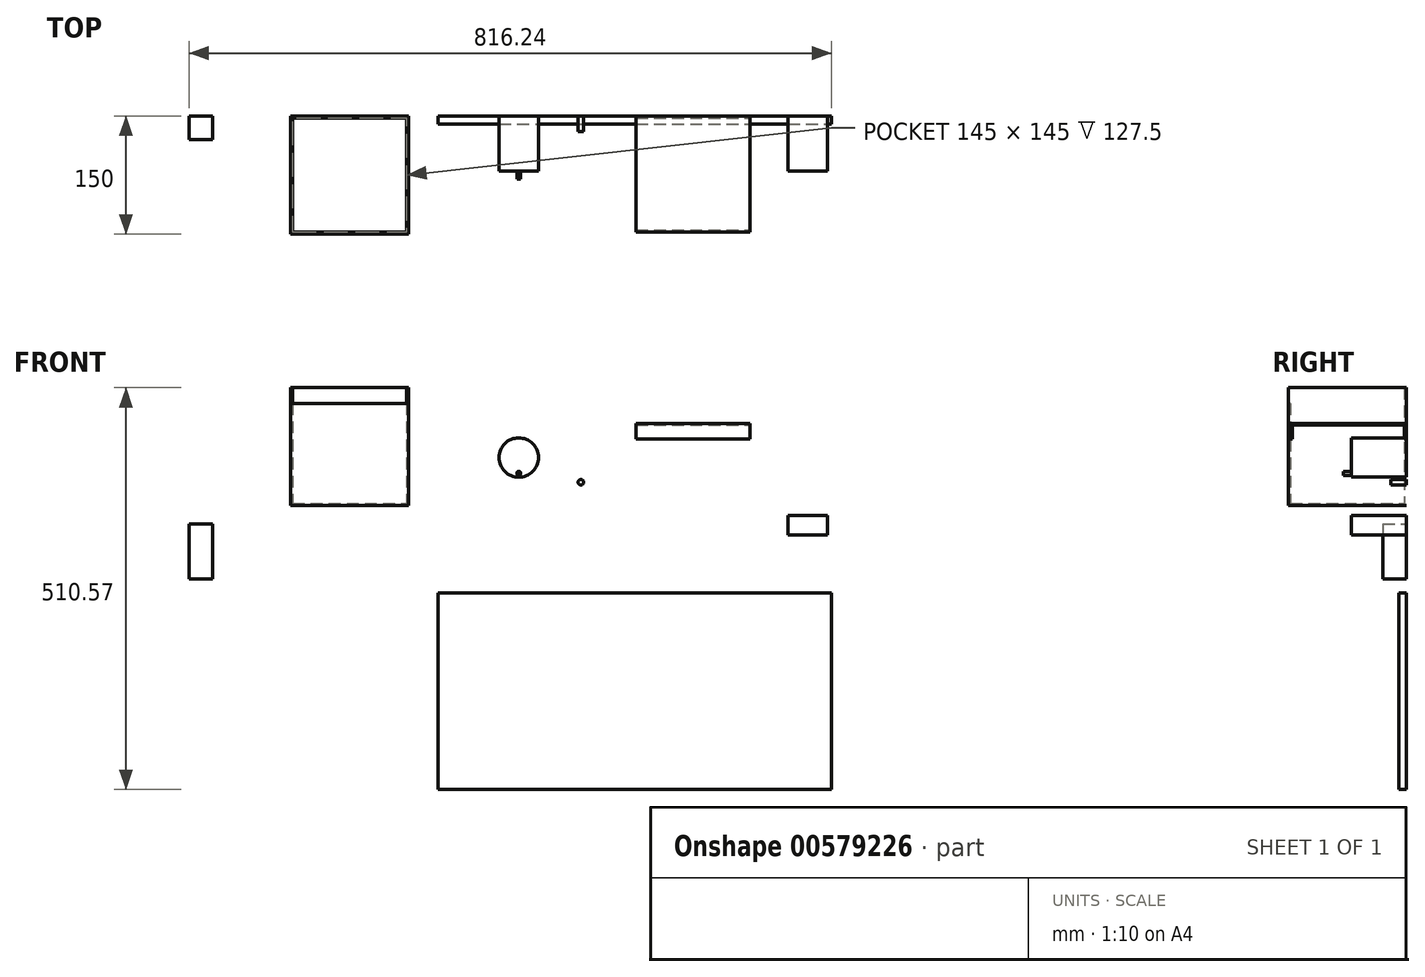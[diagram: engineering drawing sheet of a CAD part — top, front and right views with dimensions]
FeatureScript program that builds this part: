
annotation { "Feature Type Name" : "Feature", "Feature Type Description" : "" }
export const myFeature = defineFeature(function(context is Context, id is Id, definition is map)
    precondition{}
    {
        {
            var Q0;
            Q0=qCreatedBy(makeId("Front.planeOp"),FACE);
            var sketch = newSketch(context, id + "F0", { "sketchPlane" : qUnion([Q0])});
            skLineSegment(sketch, "E0.bottom", {"start": v(0, 0) * mm, "end": v(500, 0) * mm});
            skLineSegment(sketch, "E0.top", {"start": v(0, -250) * mm, "end": v(500, -250) * mm});
            skLineSegment(sketch, "E0.left", {"start": v(0, 0) * mm, "end": v(0, -250) * mm});
            skLineSegment(sketch, "E0.right", {"start": v(500, 0) * mm, "end": v(500, -250) * mm});
            skSolve(sketch);
        }
        {
            var Q0;
            Q0=qCreatedBy(makeId("Front.planeOp"),FACE);
            var sketch = newSketch(context, id + "F1", { "sketchPlane" : qUnion([Q0])});
            skLineSegment(sketch, "E1.bottom", {"start": v(-316.24, 87.62) * mm, "end": v(-286.24, 87.62) * mm});
            skLineSegment(sketch, "E1.top", {"start": v(-316.24, 17.62) * mm, "end": v(-286.24, 17.62) * mm});
            skLineSegment(sketch, "E1.left", {"start": v(-316.24, 87.62) * mm, "end": v(-316.24, 17.62) * mm});
            skLineSegment(sketch, "E1.right", {"start": v(-286.24, 87.62) * mm, "end": v(-286.24, 17.62) * mm});
            skSolve(sketch);
        }
        {
            var Q0;
            Q0=makeQuery(id+"F0.imprint","IMPRINT",FACE,{"disambiguationData":[TD([[makeQuery(id+"F0.imprint","IMPRINT",EDGE,{"derivedFrom":sQuery(id+"F0.wireOp",EDGE,"E0.bottom")}),-1.0]])]});
            extrude(context, id + "F2", {"entities" : qUnion([Q0]), "depth" : 10 * mm, "offsetDistance" : 25 * mm});
        }
        {
            var Q0;
            Q0 = qSketchRegion(id + "F1", true);
            extrude(context, id + "F3", {"entities" : qUnion([Q0]), "depth" : 30 * mm, "offsetDistance" : 25 * mm});
        }
        {
            var Q0;
            Q0=qCreatedBy(makeId("Front.planeOp"),FACE);
            var sketch = newSketch(context, id + "F4", { "sketchPlane" : qUnion([Q0])});
            skLineSegment(sketch, "E2.bottom", {"start": v(-187.08, 260.57) * mm, "end": v(-37.08, 260.57) * mm});
            skLineSegment(sketch, "E2.top", {"start": v(-187.08, 110.57) * mm, "end": v(-37.08, 110.57) * mm});
            skLineSegment(sketch, "E2.left", {"start": v(-187.08, 260.57) * mm, "end": v(-187.08, 110.57) * mm});
            skLineSegment(sketch, "E2.right", {"start": v(-37.08, 260.57) * mm, "end": v(-37.08, 110.57) * mm});
            skSolve(sketch);
        }
        {
            var Q0;
            Q0 = qSketchRegion(id + "F4", true);
            extrude(context, id + "F5", {"entities" : qUnion([Q0]), "depth" : 150 * mm, "offsetDistance" : 25 * mm});
        }
        {
            var Q0;
            Q0=makeQuery(id+"F5.opExtrude","SWEPT_FACE",FACE,{"disambiguationData":[OSD([sQuery(id+"F4.wireOp",EDGE,"E2.bottom")])]});
            shell(context, id + "F6", {"entities" : qUnion([Q0]), "thickness" : 2.5 * mm});
        }
        {
            var Q0;
            Q0=makeQuery(id+"F5.opExtrude","CAP_FACE",FACE,{"disambiguationData":[OSD([sQuery(id+"F4.wireOp",EDGE,"E2.bottom"),sQuery(id+"F4.wireOp",EDGE,"E2.top"),sQuery(id+"F4.wireOp",EDGE,"E2.left"),sQuery(id+"F4.wireOp",EDGE,"E2.right")])],"isStart":false});
            var sketch = newSketch(context, id + "F7", { "sketchPlane" : qUnion([Q0])});
            skPoint(sketch, "E3", {"position": v(-187.08, 260.57) * mm});
            skLineSegment(sketch, "E4", {"start": v(-112.08, 260.57) * mm, "end": v(-184.58, 260.57) * mm});
            skLineSegment(sketch, "E5", {"start": v(-184.58, 260.57) * mm, "end": v(-184.58, 240.57) * mm});
            skLineSegment(sketch, "E6", {"start": v(-39.58, 240.57) * mm, "end": v(-39.58, 260.57) * mm});
            skLineSegment(sketch, "E7", {"start": v(-184.58, 240.57) * mm, "end": v(-39.58, 240.57) * mm});
            skLineSegment(sketch, "E8", {"start": v(-184.58, 240.57) * mm, "end": v(-184.58, 260.57) * mm});
            skSolve(sketch);
        }
        {
            var Q0;
            {var subQ1=sQuery(id+"F7.wireOp",EDGE,"E4");Q0=makeQuery(id+"F7.imprint","IMPRINT",FACE,{"disambiguationData":[TD([[makeQuery(id+"F7.imprint","IMPRINT",EDGE,{"derivedFrom":subQ1}),-1.0]])]});}
            extrude(context, id + "F8", {"entities" : qUnion([Q0]), "operationType" : NewBodyOperationType.REMOVE, "oppositeDirection" : true, "depth" : 100 * mm, "offsetDistance" : 25 * mm});
        }
        {
            var Q0;
            Q0=qCreatedBy(makeId("Front.planeOp"),FACE);
            var sketch = newSketch(context, id + "F9", { "sketchPlane" : qUnion([Q0])});
            skCircle(sketch, "E9", {"center": v(102.75, 171.72) * mm, "radius": 25 * mm});
            skSolve(sketch);
        }
        {
            var Q0;
            Q0=makeQuery(id+"F9.imprint","IMPRINT",FACE,{"disambiguationData":[TD([[makeQuery(id+"F9.imprint","IMPRINT",EDGE,{"derivedFrom":sQuery(id+"F9.wireOp",EDGE,"E9")}),1.0]])]});
            extrude(context, id + "F10", {"entities" : qUnion([Q0]), "depth" : 70 * mm, "offsetDistance" : 25 * mm});
        }
        {
            var Q0;
            Q0=makeQuery(id+"F10.opExtrude","CAP_FACE",FACE,{"disambiguationData":[OSD([sQuery(id+"F9.wireOp",EDGE,"E9")])],"isStart":false});
            var sketch = newSketch(context, id + "F11", { "sketchPlane" : qUnion([Q0])});
            skCircle(sketch, "E10", {"center": v(102.75, 151.72) * mm, "radius": 2.5 * mm});
            skSolve(sketch);
        }
        {
            var Q0;
            Q0=makeQuery(id+"F11.imprint","IMPRINT",FACE,{"disambiguationData":[TD([[makeQuery(id+"F11.imprint","IMPRINT",EDGE,{"derivedFrom":sQuery(id+"F11.wireOp",EDGE,"E10")}),1.0]])]});
            extrude(context, id + "F12", {"entities" : qUnion([Q0]), "operationType" : NewBodyOperationType.ADD, "depth" : 10 * mm, "offsetDistance" : 25 * mm});
        }
        {
            var Q0;
            Q0=qCreatedBy(makeId("Front.planeOp"),FACE);
            var sketch = newSketch(context, id + "F13", { "sketchPlane" : qUnion([Q0])});
            skLineSegment(sketch, "E11.bottom", {"start": v(251.7, 215.24) * mm, "end": v(396.7, 215.24) * mm});
            skLineSegment(sketch, "E11.top", {"start": v(251.7, 195.24) * mm, "end": v(396.7, 195.24) * mm});
            skLineSegment(sketch, "E11.left", {"start": v(251.7, 215.24) * mm, "end": v(251.7, 195.24) * mm});
            skLineSegment(sketch, "E11.right", {"start": v(396.7, 215.24) * mm, "end": v(396.7, 195.24) * mm});
            skSolve(sketch);
        }
        {
            var Q0;
            Q0 = qSketchRegion(id + "F13", true);
            extrude(context, id + "F14", {"entities" : qUnion([Q0]), "depth" : 147.5 * mm, "offsetDistance" : 25 * mm});
        }
        {
            var Q0;
            Q0=makeQuery(id+"F14.opExtrude","SWEPT_FACE",FACE,{"disambiguationData":[OSD([sQuery(id+"F13.wireOp",EDGE,"E11.right")])]});
            var Q1;
            Q1=makeQuery(id+"F14.opExtrude","SWEPT_FACE",FACE,{"disambiguationData":[OSD([sQuery(id+"F13.wireOp",EDGE,"E11.left")])]});
            var Q2;
            Q2=makeQuery(id+"F14.opExtrude","SWEPT_FACE",FACE,{"disambiguationData":[OSD([sQuery(id+"F13.wireOp",EDGE,"E11.top")])]});
            shell(context, id + "F15", {"entities" : qUnion([Q0, Q1, Q2]), "thickness" : 2.5 * mm});
        }
        {
            var Q0;
            Q0=qCreatedBy(makeId("Front.planeOp"),FACE);
            var sketch = newSketch(context, id + "F16", { "sketchPlane" : qUnion([Q0])});
            skCircle(sketch, "E12", {"center": v(181.62, 140.38) * mm, "radius": 3.5 * mm});
            skSolve(sketch);
        }
        {
            var Q0;
            Q0=makeQuery(id+"F16.imprint","IMPRINT",FACE,{"disambiguationData":[TD([[makeQuery(id+"F16.imprint","IMPRINT",EDGE,{"derivedFrom":sQuery(id+"F16.wireOp",EDGE,"E12")}),1.0]])]});
            extrude(context, id + "F17", {"entities" : qUnion([Q0]), "depth" : 20 * mm, "offsetDistance" : 25 * mm});
        }
        {
            var Q0;
            Q0=qCreatedBy(makeId("Front.planeOp"),FACE);
            var sketch = newSketch(context, id + "F18", { "sketchPlane" : qUnion([Q0])});
            skLineSegment(sketch, "E13.bottom", {"start": v(444.69, 98.1) * mm, "end": v(494.69, 98.1) * mm});
            skLineSegment(sketch, "E13.top", {"start": v(444.69, 73.1) * mm, "end": v(494.69, 73.1) * mm});
            skLineSegment(sketch, "E13.left", {"start": v(444.69, 98.1) * mm, "end": v(444.69, 73.1) * mm});
            skLineSegment(sketch, "E13.right", {"start": v(494.69, 98.1) * mm, "end": v(494.69, 73.1) * mm});
            skSolve(sketch);
        }
        {
            var Q0;
            Q0=makeQuery(id+"F18.imprint","IMPRINT",FACE,{"disambiguationData":[TD([[makeQuery(id+"F18.imprint","IMPRINT",EDGE,{"derivedFrom":sQuery(id+"F18.wireOp",EDGE,"E13.bottom")}),-1.0]])]});
            extrude(context, id + "F19", {"entities" : qUnion([Q0]), "depth" : 70 * mm, "offsetDistance" : 25 * mm});
        }
    });
